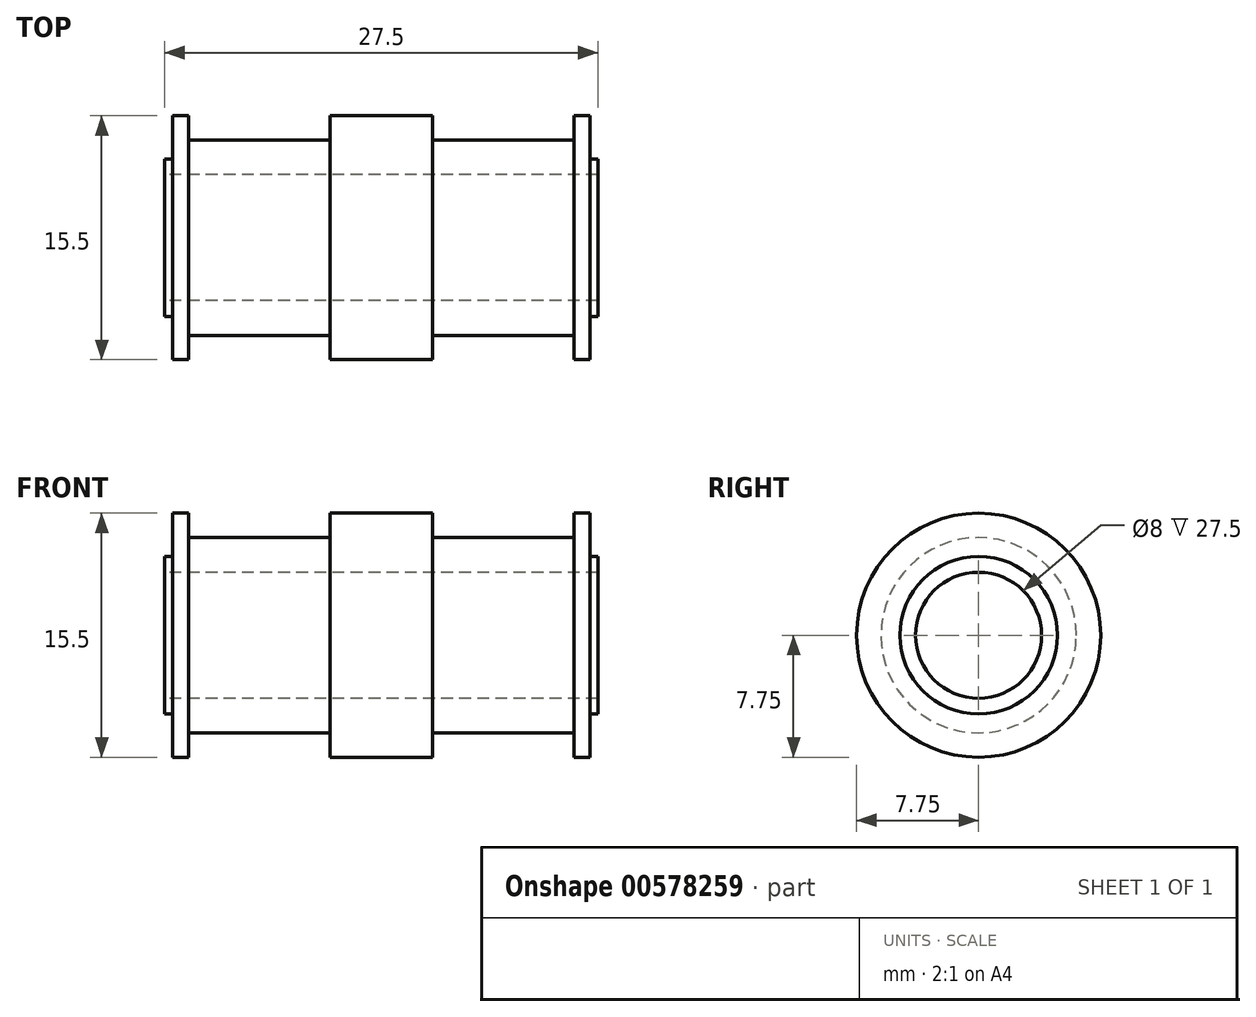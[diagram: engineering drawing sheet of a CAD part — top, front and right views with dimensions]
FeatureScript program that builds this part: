
annotation { "Feature Type Name" : "Feature", "Feature Type Description" : "" }
export const myFeature = defineFeature(function(context is Context, id is Id, definition is map)
    precondition{}
    {
        {
            var Q0;
            Q0=qCreatedBy(makeId("Right.planeOp"),FACE);
            var sketch = newSketch(context, id + "F0", { "sketchPlane" : qUnion([Q0])});
            skCircle(sketch, "E0", {"center": v(0, 0) * mm, "radius": 5 * mm});
            skCircle(sketch, "E1", {"center": v(0, 0) * mm, "radius": 4 * mm});
            skSolve(sketch);
        }
        {
            var Q0;
            Q0 = qSketchRegion(id + "F0", true);
            extrude(context, id + "F1", {"entities" : qUnion([Q0]), "depth" : 0.5 * mm, "offsetDistance" : 25 * mm});
        }
        {
            var Q0;
            Q0=makeQuery(id+"F1.opExtrude","CAP_FACE",FACE,{"disambiguationData":[OSD([sQuery(id+"F0.wireOp",EDGE,"E0"),sQuery(id+"F0.wireOp",EDGE,"E1")])],"isStart":false});
            var sketch = newSketch(context, id + "F2", { "sketchPlane" : qUnion([Q0])});
            skCircle(sketch, "E2", {"center": v(0, 0) * mm, "radius": 7.75 * mm});
            skSolve(sketch);
        }
        {
            var Q0;
            Q0=makeQuery(id+"F2.imprint","IMPRINT",FACE,{"disambiguationData":[TD([[makeQuery(id+"F2.imprint","IMPRINT",EDGE,{"derivedFrom":sQuery(id+"F2.wireOp",EDGE,"E2")}),1.0]])]});
            var Q1;
            Q1=makeQuery(id+"F2.imprint","IMPRINT",FACE,{"disambiguationData":[TD([[makeQuery(id+"F2.imprint","IMPRINT",EDGE,{"derivedFrom":makeQuery(id+"F1.opExtrude","CAP_EDGE",EDGE,{"disambiguationData":[OSD([sQuery(id+"F0.wireOp",EDGE,"E0")])],"isStart":false})}),1.0]])]});
            extrude(context, id + "F3", {"entities" : qUnion([Q0, Q1]), "depth" : 1 * mm, "offsetDistance" : 25 * mm});
        }
        {
            var Q0;
            Q0=makeQuery(id+"F3.opExtrude","CAP_FACE",FACE,{"disambiguationData":[OSD([sQuery(id+"F0.wireOp",EDGE,"E1"),sQuery(id+"F2.wireOp",EDGE,"E2")])],"isStart":false});
            var sketch = newSketch(context, id + "F4", { "sketchPlane" : qUnion([Q0])});
            skCircle(sketch, "E3", {"center": v(0, 0) * mm, "radius": 6.2 * mm});
            skSolve(sketch);
        }
        {
            var Q0;
            Q0=makeQuery(id+"F4.imprint","IMPRINT",FACE,{"disambiguationData":[TD([[makeQuery(id+"F4.imprint","IMPRINT",EDGE,{"derivedFrom":sQuery(id+"F4.wireOp",EDGE,"E3")}),1.0]])]});
            extrude(context, id + "F5", {"entities" : qUnion([Q0]), "operationType" : NewBodyOperationType.ADD, "depth" : 9 * mm, "offsetDistance" : 25 * mm});
        }
        {
            var Q0;
            Q0=makeQuery(id+"F5.opExtrude","CAP_FACE",FACE,{"disambiguationData":[OSD([sQuery(id+"F0.wireOp",EDGE,"E1"),sQuery(id+"F4.wireOp",EDGE,"E3")])],"isStart":false});
            var sketch = newSketch(context, id + "F6", { "sketchPlane" : qUnion([Q0])});
            skCircle(sketch, "E4", {"center": v(0, 0) * mm, "radius": 4 * mm});
            skCircle(sketch, "E5", {"center": v(0, 0) * mm, "radius": 7.75 * mm});
            skSolve(sketch);
        }
        {
            var Q0;
            Q0 = qSketchRegion(id + "F6", true);
            extrude(context, id + "F7", {"entities" : qUnion([Q0]), "depth" : 3.25 * mm, "offsetDistance" : 25 * mm});
        }
        {
            var Q0;
            Q0=makeQuery(id+"F3.opExtrude","SWEPT_BODY",BODY,{"disambiguationData":[OSD([sQuery(id+"F0.wireOp",EDGE,"E1"),sQuery(id+"F2.wireOp",EDGE,"E2")])]});
            var Q1;
            Q1=makeQuery(id+"F1.opExtrude","SWEPT_BODY",BODY,{"disambiguationData":[OSD([sQuery(id+"F0.wireOp",EDGE,"E0"),sQuery(id+"F0.wireOp",EDGE,"E1")])]});
            var Q2;
            Q2=makeQuery(id+"F7.opExtrude","SWEPT_BODY",BODY,{"disambiguationData":[OSD([sQuery(id+"F6.wireOp",EDGE,"E4"),sQuery(id+"F6.wireOp",EDGE,"E5")])]});
            var Q3;
            Q3=makeQuery(id+"F7.opExtrude","CAP_FACE",FACE,{"disambiguationData":[OSD([sQuery(id+"F6.wireOp",EDGE,"E4"),sQuery(id+"F6.wireOp",EDGE,"E5")])],"isStart":false});
            mirror(context, id + "F8", {"operationType" : NewBodyOperationType.ADD, "entities" : qUnion([Q0, Q1, Q2]), "mirrorPlane" : qUnion([Q3])});
        }
    });
